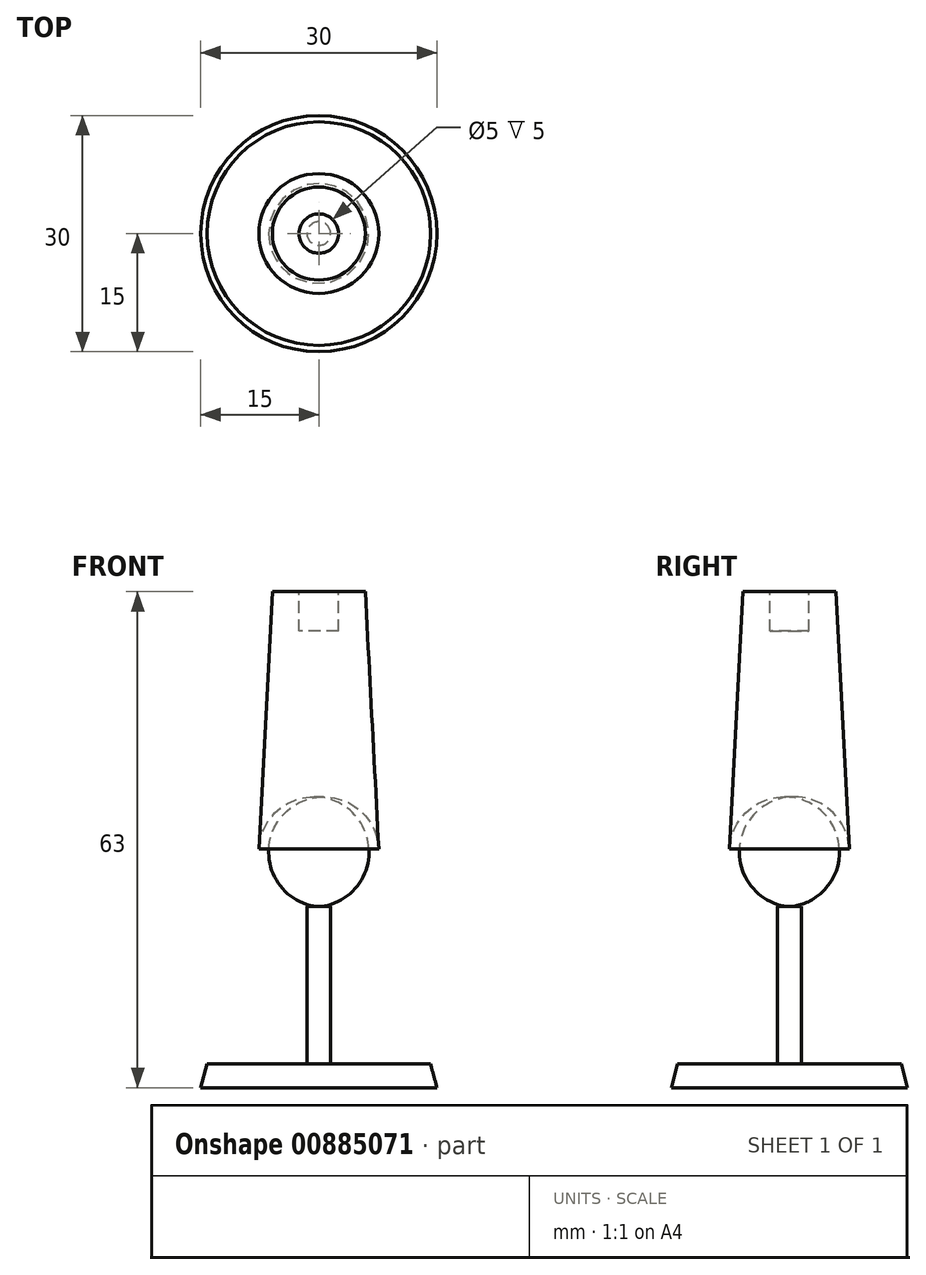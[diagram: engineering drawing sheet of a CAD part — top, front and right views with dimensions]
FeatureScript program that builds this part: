
annotation { "Feature Type Name" : "Feature", "Feature Type Description" : "" }
export const myFeature = defineFeature(function(context is Context, id is Id, definition is map)
    precondition{}
    {
        {
            var Q0;
            Q0=qCreatedBy(makeId("Top.planeOp"),FACE);
            var sketch = newSketch(context, id + "F0", { "sketchPlane" : qUnion([Q0])});
            skCircle(sketch, "E0", {"center": v(0, 0) * mm, "radius": 15 * mm});
            skSolve(sketch);
        }
        {
            var Q0;
            Q0 = qSketchRegion(id + "F0", true);
            extrude(context, id + "F1", {"entities" : qUnion([Q0]), "depth" : 3 * mm, "offsetDistance" : 25 * mm, "hasDraft" : true, "draftAngle" : 15 * degree, "draftPullDirection" : true});
        }
        {
            var Q0;
            Q0=makeQuery(id+"F1.opExtrude","CAP_FACE",FACE,{"disambiguationData":[OSD([sQuery(id+"F0.wireOp",EDGE,"E0")])],"isStart":false});
            var sketch = newSketch(context, id + "F2", { "sketchPlane" : qUnion([Q0])});
            skCircle(sketch, "E1", {"center": v(0, 0) * mm, "radius": 1.5 * mm});
            skSolve(sketch);
        }
        {
            var Q0;
            Q0 = qSketchRegion(id + "F2", true);
            extrude(context, id + "F3", {"entities" : qUnion([Q0]), "operationType" : NewBodyOperationType.ADD, "depth" : 20 * mm, "offsetDistance" : 25 * mm});
        }
        {
            var Q0;
            Q0=makeQuery(id+"F3.opExtrude","CAP_FACE",FACE,{"disambiguationData":[OSD([sQuery(id+"F2.wireOp",EDGE,"E1")])],"isStart":false});
            var sketch = newSketch(context, id + "F4", { "sketchPlane" : qUnion([Q0])});
            skCircle(sketch, "E2", {"center": v(0, 0) * mm, "radius": 8 * mm});
            skSolve(sketch);
        }
        {
            var Q0;
            Q0 = qSketchRegion(id + "F4", true);
            extrude(context, id + "F5", {"entities" : qUnion([Q0]), "operationType" : NewBodyOperationType.ADD, "depth" : 40 * mm, "offsetDistance" : 25 * mm, "hasDraft" : true, "draftAngle" : 3 * degree, "draftPullDirection" : true});
        }
        {
            var Q0;
            Q0=makeQuery(id+"F5.opExtrude","CAP_FACE",FACE,{"disambiguationData":[OSD([sQuery(id+"F4.wireOp",EDGE,"E2")])],"isStart":false});
            var sketch = newSketch(context, id + "F6", { "sketchPlane" : qUnion([Q0])});
            skCircle(sketch, "E3", {"center": v(0, 0) * mm, "radius": 2.5 * mm});
            skSolve(sketch);
        }
        {
            var Q0;
            Q0=makeQuery(id+"F6.imprint","IMPRINT",FACE,{"disambiguationData":[TD([[makeQuery(id+"F6.imprint","IMPRINT",EDGE,{"derivedFrom":sQuery(id+"F6.wireOp",EDGE,"E3")}),1.0]])]});
            extrude(context, id + "F7", {"entities" : qUnion([Q0]), "operationType" : NewBodyOperationType.REMOVE, "oppositeDirection" : true, "depth" : 5 * mm, "offsetDistance" : 25 * mm});
        }
        {
            var Q0;
            Q0=makeQuery(id+"F5.opExtrude","CAP_EDGE",EDGE,{"disambiguationData":[OSD([sQuery(id+"F4.wireOp",EDGE,"E2")])],"isStart":true});
            fillet(context, id + "F8", {"entities" : qUnion([Q0]), "radius" : 7 * mm, "tangentPropagation" : true, "allowEdgeOverflow" : false});
        }
    });
